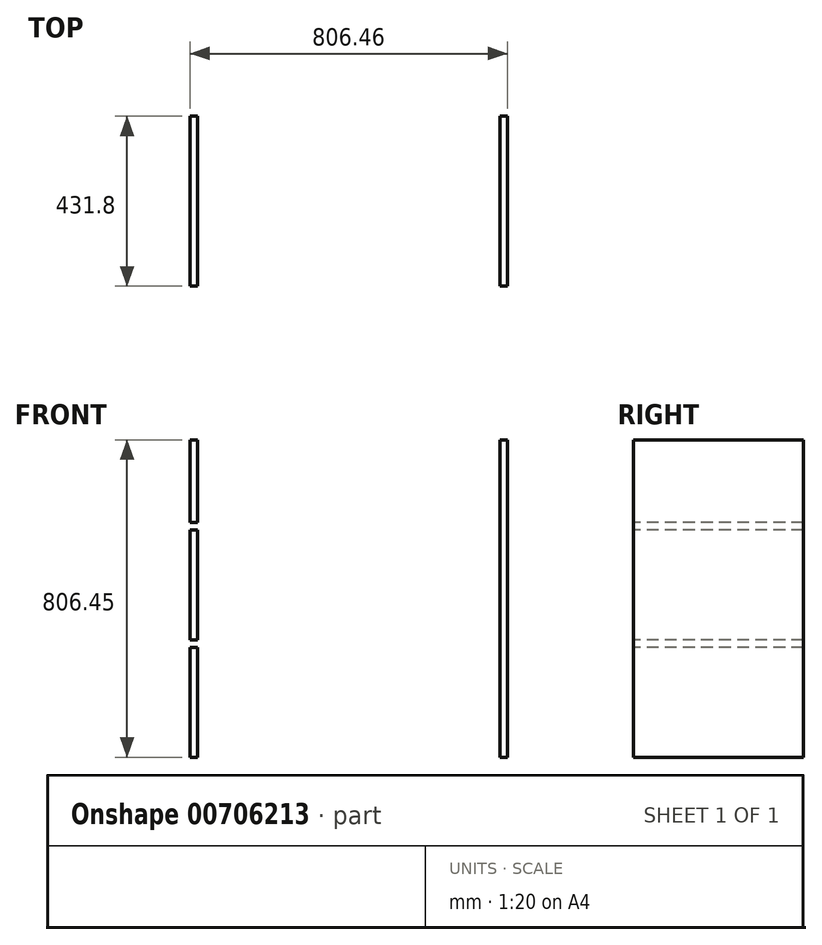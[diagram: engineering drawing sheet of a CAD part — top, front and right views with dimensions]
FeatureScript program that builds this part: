
annotation { "Feature Type Name" : "Feature", "Feature Type Description" : "" }
export const myFeature = defineFeature(function(context is Context, id is Id, definition is map)
    precondition{}
    {
        {
            var Q0;
            Q0=qCreatedBy(makeId("Front.planeOp"),FACE);
            var sketch = newSketch(context, id + "F0", { "sketchPlane" : qUnion([Q0])});
            skLineSegment(sketch, "E0", {"start": v(-403.23, 410.44) * mm, "end": v(403.23, 410.44) * mm});
            skLineSegment(sketch, "E1", {"start": v(-403.22, -396.01) * mm, "end": v(403.22, -396.01) * mm});
            skLineSegment(sketch, "E2.bottom", {"start": v(-403.23, 410.44) * mm, "end": v(403.22, 410.44) * mm});
            skLineSegment(sketch, "E2.top", {"start": v(-403.23, -396.01) * mm, "end": v(403.22, -396.01) * mm});
            skLineSegment(sketch, "E2.left", {"start": v(-403.23, 410.44) * mm, "end": v(-403.23, -396.01) * mm});
            skLineSegment(sketch, "E2.right", {"start": v(403.22, 410.44) * mm, "end": v(403.22, -396.01) * mm});
            skLineSegment(sketch, "E3", {"start": v(-162.1, 200.89) * mm, "end": v(403.22, 200.89) * mm});
            skLineSegment(sketch, "E4", {"start": v(-162.1, 181.84) * mm, "end": v(403.22, 181.84) * mm});
            skLineSegment(sketch, "E5", {"start": v(-162.1, -97.56) * mm, "end": v(403.22, -97.56) * mm});
            skLineSegment(sketch, "E6", {"start": v(-162.1, -116.61) * mm, "end": v(-403.23, -116.61) * mm});
            skLineSegment(sketch, "E7.bottom", {"start": v(-403.23, -116.61) * mm, "end": v(403.22, -116.61) * mm});
            skLineSegment(sketch, "E7.top", {"start": v(-403.23, -97.56) * mm, "end": v(403.22, -97.56) * mm});
            skLineSegment(sketch, "E7.left", {"start": v(-403.23, -116.61) * mm, "end": v(-403.23, -97.56) * mm});
            skLineSegment(sketch, "E7.right", {"start": v(403.22, -116.61) * mm, "end": v(403.22, -97.56) * mm});
            skLineSegment(sketch, "E8", {"start": v(-162.1, 181.84) * mm, "end": v(-403.23, 181.84) * mm});
            skLineSegment(sketch, "E9.bottom", {"start": v(-403.23, 181.84) * mm, "end": v(403.22, 181.84) * mm});
            skLineSegment(sketch, "E9.top", {"start": v(-403.23, 200.89) * mm, "end": v(403.22, 200.89) * mm});
            skLineSegment(sketch, "E9.left", {"start": v(-403.23, 181.84) * mm, "end": v(-403.23, 200.89) * mm});
            skLineSegment(sketch, "E9.right", {"start": v(403.22, 181.84) * mm, "end": v(403.22, 200.89) * mm});
            skLineSegment(sketch, "E10.0", {"start": v(-403.23, 391.39) * mm, "end": v(403.22, 391.39) * mm});
            skLineSegment(sketch, "E11.0", {"start": v(-384.18, 410.44) * mm, "end": v(-384.18, -396.01) * mm});
            skLineSegment(sketch, "E12.0", {"start": v(384.18, 410.44) * mm, "end": v(384.18, -396.01) * mm});
            skSolve(sketch);
        }
        {
            var Q0;
            {var subQ1=sQuery(id+"F0.wireOp",EDGE,"E2.left");var subQ3=sQuery(id+"F0.wireOp",EDGE,"E10.0");var subQ4=makeQuery(id+"F0.imprint","INTERSECT",VERTEX,{"derivedFrom":[subQ1,subQ3]});Q0=makeQuery(id+"F0.imprint","IMPRINT",FACE,{"disambiguationData":[TD([[makeQuery(id+"F0.imprint","IMPRINT",EDGE,{"disambiguationData":[TD([[subQ4,-1.0]])],"derivedFrom":subQ3}),-1.0]])]});}
            var Q1;
            {var subQ0=sQuery(id+"F0.wireOp",EDGE,"E9.top");var subQ1=makeQuery(id+"F0.imprint","IMPRINT",VERTEX,{"derivedFrom":subQ0});Q1=makeQuery(id+"F0.imprint","IMPRINT",FACE,{"disambiguationData":[TD([[makeQuery(id+"F0.imprint","IMPRINT",EDGE,{"disambiguationData":[TD([[subQ1,1.0]])],"derivedFrom":subQ0}),-1.0]])]});}
            var Q2;
            {var subQ0=sQuery(id+"F0.wireOp",EDGE,"E9.left");Q2=makeQuery(id+"F0.imprint","IMPRINT",FACE,{"disambiguationData":[TD([[makeQuery(id+"F0.imprint","IMPRINT",EDGE,{"derivedFrom":subQ0}),-1.0]])]});}
            var Q3;
            {var subQ0=sQuery(id+"F0.wireOp",EDGE,"E7.top");var subQ5=sQuery(id+"F0.wireOp",EDGE,"E11.0");var subQ6=makeQuery(id+"F0.imprint","INTERSECT",VERTEX,{"derivedFrom":[subQ0,subQ5]});Q3=makeQuery(id+"F0.imprint","IMPRINT",FACE,{"disambiguationData":[TD([[makeQuery(id+"F0.imprint","IMPRINT",EDGE,{"disambiguationData":[TD([[subQ6,1.0]])],"derivedFrom":subQ5}),-1.0]])]});}
            var Q4;
            {var subQ0=sQuery(id+"F0.wireOp",EDGE,"E7.left");Q4=makeQuery(id+"F0.imprint","IMPRINT",FACE,{"disambiguationData":[TD([[makeQuery(id+"F0.imprint","IMPRINT",EDGE,{"derivedFrom":subQ0}),-1.0]])]});}
            var Q5;
            {var subQ0=sQuery(id+"F0.wireOp",EDGE,"E2.left");var subQ1=sQuery(id+"F0.wireOp",EDGE,"E2.top");var subQ2=makeQuery(id+"F0.imprint","INTERSECT",VERTEX,{"derivedFrom":[subQ1,subQ0]});Q5=makeQuery(id+"F0.imprint","IMPRINT",FACE,{"disambiguationData":[TD([[makeQuery(id+"F0.imprint","IMPRINT",EDGE,{"disambiguationData":[TD([[subQ2,-1.0]])],"derivedFrom":subQ1}),1.0]])]});}
            var Q6;
            {var subQ4=sQuery(id+"F0.wireOp",EDGE,"E7.bottom");var subQ5=makeQuery(id+"F0.imprint","IMPRINT",VERTEX,{"derivedFrom":subQ4});Q6=makeQuery(id+"F0.imprint","IMPRINT",FACE,{"disambiguationData":[TD([[makeQuery(id+"F0.imprint","IMPRINT",EDGE,{"disambiguationData":[TD([[subQ5,1.0]])],"derivedFrom":subQ4}),1.0]])]});}
            var Q7;
            {var subQ1=sQuery(id+"F0.wireOp",EDGE,"E2.right");var subQ3=sQuery(id+"F0.wireOp",EDGE,"E10.0");var subQ4=makeQuery(id+"F0.imprint","INTERSECT",VERTEX,{"derivedFrom":[subQ1,subQ3]});Q7=makeQuery(id+"F0.imprint","IMPRINT",FACE,{"disambiguationData":[TD([[makeQuery(id+"F0.imprint","IMPRINT",EDGE,{"disambiguationData":[TD([[subQ4,1.0]])],"derivedFrom":subQ3}),-1.0]])]});}
            var Q8;
            {var subQ0=sQuery(id+"F0.wireOp",EDGE,"E9.right");Q8=makeQuery(id+"F0.imprint","IMPRINT",FACE,{"disambiguationData":[TD([[makeQuery(id+"F0.imprint","IMPRINT",EDGE,{"derivedFrom":subQ0}),1.0]])]});}
            var Q9;
            {var subQ0=sQuery(id+"F0.wireOp",EDGE,"E7.top");var subQ5=sQuery(id+"F0.wireOp",EDGE,"E12.0");var subQ6=makeQuery(id+"F0.imprint","INTERSECT",VERTEX,{"derivedFrom":[subQ0,subQ5]});Q9=makeQuery(id+"F0.imprint","IMPRINT",FACE,{"disambiguationData":[TD([[makeQuery(id+"F0.imprint","IMPRINT",EDGE,{"disambiguationData":[TD([[subQ6,1.0]])],"derivedFrom":subQ5}),1.0]])]});}
            var Q10;
            {var subQ0=sQuery(id+"F0.wireOp",EDGE,"E2.right");var subQ1=sQuery(id+"F0.wireOp",EDGE,"E2.top");var subQ2=makeQuery(id+"F0.imprint","INTERSECT",VERTEX,{"derivedFrom":[subQ1,subQ0]});Q10=makeQuery(id+"F0.imprint","IMPRINT",FACE,{"disambiguationData":[TD([[makeQuery(id+"F0.imprint","IMPRINT",EDGE,{"disambiguationData":[TD([[subQ2,1.0]])],"derivedFrom":subQ1}),1.0]])]});}
            var Q11;
            {var subQ0=sQuery(id+"F0.wireOp",EDGE,"E7.right");Q11=makeQuery(id+"F0.imprint","IMPRINT",FACE,{"disambiguationData":[TD([[makeQuery(id+"F0.imprint","IMPRINT",EDGE,{"derivedFrom":subQ0}),1.0]])]});}
            var Q12;
            {var subQ0=sQuery(id+"F0.wireOp",EDGE,"E2.right");var subQ1=sQuery(id+"F0.wireOp",EDGE,"E2.bottom");var subQ2=makeQuery(id+"F0.imprint","INTERSECT",VERTEX,{"derivedFrom":[subQ1,subQ0]});Q12=makeQuery(id+"F0.imprint","IMPRINT",FACE,{"disambiguationData":[TD([[makeQuery(id+"F0.imprint","IMPRINT",EDGE,{"disambiguationData":[TD([[subQ2,1.0]])],"derivedFrom":subQ1}),-1.0]])]});}
            var Q13;
            {var subQ0=sQuery(id+"F0.wireOp",EDGE,"E2.left");var subQ1=sQuery(id+"F0.wireOp",EDGE,"E2.bottom");var subQ2=makeQuery(id+"F0.imprint","INTERSECT",VERTEX,{"derivedFrom":[subQ1,subQ0]});Q13=makeQuery(id+"F0.imprint","IMPRINT",FACE,{"disambiguationData":[TD([[makeQuery(id+"F0.imprint","IMPRINT",EDGE,{"disambiguationData":[TD([[subQ2,-1.0]])],"derivedFrom":subQ1}),-1.0]])]});}
            extrude(context, id + "F1", {"entities" : qUnion([Q0, Q1, Q2, Q3, Q4, Q5, Q6, Q7, Q8, Q9, Q10, Q11, Q12, Q13]), "oppositeDirection" : true, "depth" : 431.8 * mm, "offsetDistance" : 25.4 * mm});
        }
    });
